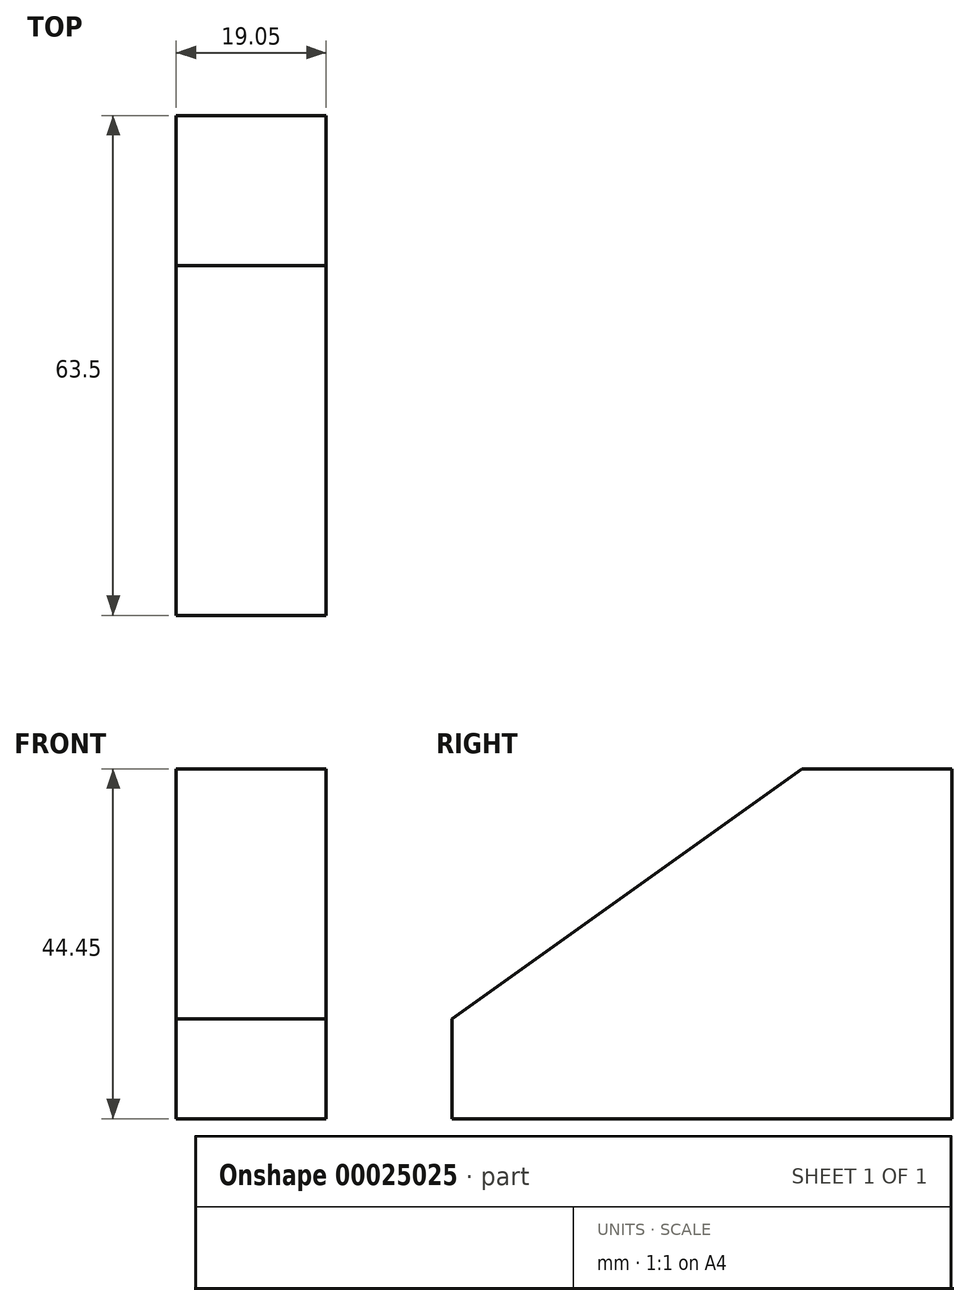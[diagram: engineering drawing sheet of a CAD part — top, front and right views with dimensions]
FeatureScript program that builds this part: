
annotation { "Feature Type Name" : "Feature", "Feature Type Description" : "" }
export const myFeature = defineFeature(function(context is Context, id is Id, definition is map)
    precondition{}
    {
        {
            var Q0;
            Q0=qCreatedBy(makeId("Right.planeOp"),FACE);
            var sketch = newSketch(context, id + "F0", { "sketchPlane" : qUnion([Q0])});
            skLineSegment(sketch, "E0", {"start": v(-58.44, -6.92) * mm, "end": v(5.06, -6.92) * mm});
            skLineSegment(sketch, "E1", {"start": v(5.06, -6.92) * mm, "end": v(5.06, 37.53) * mm});
            skLineSegment(sketch, "E2", {"start": v(-58.44, -6.92) * mm, "end": v(-58.44, 5.78) * mm});
            skLineSegment(sketch, "E3", {"start": v(5.06, 37.53) * mm, "end": v(-14, 37.53) * mm});
            skLineSegment(sketch, "E4", {"start": v(-58.44, 5.78) * mm, "end": v(-14, 37.53) * mm});
            skSolve(sketch);
        }
        {
            var Q0;
            Q0 = qSketchRegion(id + "F0", true);
            extrude(context, id + "F1", {"entities" : qUnion([Q0]), "depth" : 19.05 * mm});
        }
    });
